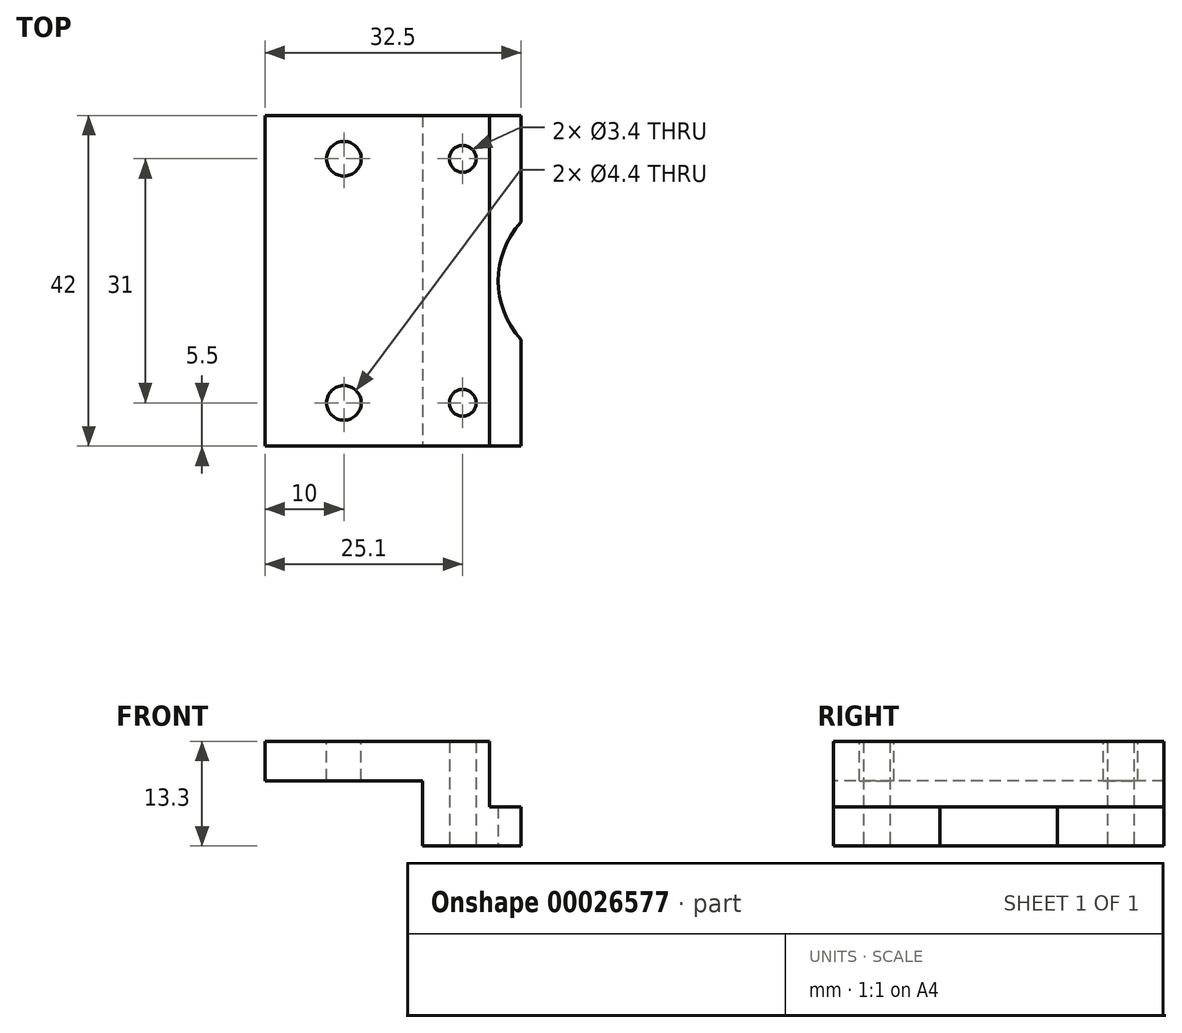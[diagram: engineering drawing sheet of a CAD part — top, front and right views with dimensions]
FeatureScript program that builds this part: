
annotation { "Feature Type Name" : "Feature", "Feature Type Description" : "" }
export const myFeature = defineFeature(function(context is Context, id is Id, definition is map)
    precondition{}
    {
        {
            var Q0;
            Q0=qCreatedBy(makeId("Front.planeOp"),FACE);
            var sketch = newSketch(context, id + "F0", { "sketchPlane" : qUnion([Q0])});
            skLineSegment(sketch, "E0", {"start": v(8.5, 13.3) * mm, "end": v(8.5, 5) * mm});
            skLineSegment(sketch, "E1", {"start": v(8.5, 5) * mm, "end": v(12.5, 5) * mm});
            skLineSegment(sketch, "E2", {"start": v(12.5, 5) * mm, "end": v(12.5, 0) * mm});
            skLineSegment(sketch, "E3", {"start": v(12.5, 0) * mm, "end": v(0, 0) * mm});
            skLineSegment(sketch, "E4", {"start": v(0, 0) * mm, "end": v(0, 13.3) * mm});
            skLineSegment(sketch, "E5", {"start": v(0, 13.3) * mm, "end": v(8.5, 13.3) * mm});
            skSolve(sketch);
        }
        {
            var Q0;
            Q0=qSketchRegion(id+"F0",true);
            extrude(context, id + "F1", {"entities" : qUnion([Q0]), "oppositeDirection" : true, "depth" : 42 * mm});
        }
        {
            var Q0;
            Q0=makeQuery(id+"F1.opExtrude","SWEPT_FACE",FACE,{"disambiguationData":[OSD([sQuery(id+"F0.wireOp",EDGE,"E3")])]});
            var sketch = newSketch(context, id + "F2", { "sketchPlane" : qUnion([Q0])});
            skCircle(sketch, "E6", {"center": v(5.1, -5.5) * mm, "radius": 1.7 * mm});
            skCircle(sketch, "E7", {"center": v(5.1, -36.5) * mm, "radius": 1.7 * mm});
            skCircle(sketch, "E8", {"center": v(20.6, -21) * mm, "radius": 11 * mm});
            skLineSegment(sketch, "E9", {"start": v(0, -21) * mm, "end": v(12.5, -21) * mm, "construction": true});
            skSolve(sketch);
        }
        {
            var Q0;
            Q0=qSketchRegion(id+"F2",true);
            extrude(context, id + "F3", {"entities" : qUnion([Q0]), "operationType" : NewBodyOperationType.REMOVE, "endBound" : BoundingType.THROUGH_ALL, "oppositeDirection" : true, "depth" : 25 * mm});
        }
        {
            var Q0;
            Q0=makeQuery(id+"F1.opExtrude","SWEPT_FACE",FACE,{"disambiguationData":[OSD([sQuery(id+"F0.wireOp",EDGE,"E4")])]});
            var sketch = newSketch(context, id + "F4", { "sketchPlane" : qUnion([Q0])});
            skLineSegment(sketch, "E10.bottom", {"start": v(-42, 13.3) * mm, "end": v(0, 13.3) * mm});
            skLineSegment(sketch, "E10.top", {"start": v(-42, 8.3) * mm, "end": v(0, 8.3) * mm});
            skLineSegment(sketch, "E10.left", {"start": v(-42, 13.3) * mm, "end": v(-42, 8.3) * mm});
            skLineSegment(sketch, "E10.right", {"start": v(0, 13.3) * mm, "end": v(0, 8.3) * mm});
            skSolve(sketch);
        }
        {
            var Q0;
            Q0=qSketchRegion(id+"F4",true);
            extrude(context, id + "F5", {"entities" : qUnion([Q0]), "operationType" : NewBodyOperationType.ADD, "depth" : 20 * mm});
        }
        {
            var Q0;
            Q0=makeQuery(id+"F5.boolean.opBoolean","MERGE",FACE,{"derivedFrom":[makeQuery(id+"F1.opExtrude","SWEPT_FACE",FACE,{"disambiguationData":[OSD([sQuery(id+"F0.wireOp",EDGE,"E5")])]}),makeQuery(id+"F5.opExtrude","SWEPT_FACE",FACE,{"disambiguationData":[OSD([sQuery(id+"F4.wireOp",EDGE,"E10.bottom")])]})]});
            var sketch = newSketch(context, id + "F6", { "sketchPlane" : qUnion([Q0])});
            skCircle(sketch, "E11", {"center": v(-10, 36.5) * mm, "radius": 2.2 * mm});
            skCircle(sketch, "E12", {"center": v(-10, 5.5) * mm, "radius": 2.2 * mm});
            skPoint(sketch, "E13", {"position": v(5.1, 36.5) * mm});
            skPoint(sketch, "E14", {"position": v(5.1, 5.5) * mm});
            skSolve(sketch);
        }
        {
            var Q0;
            Q0=qSketchRegion(id+"F6",true);
            extrude(context, id + "F7", {"entities" : qUnion([Q0]), "operationType" : NewBodyOperationType.REMOVE, "oppositeDirection" : true, "depth" : 25 * mm});
        }
    });
